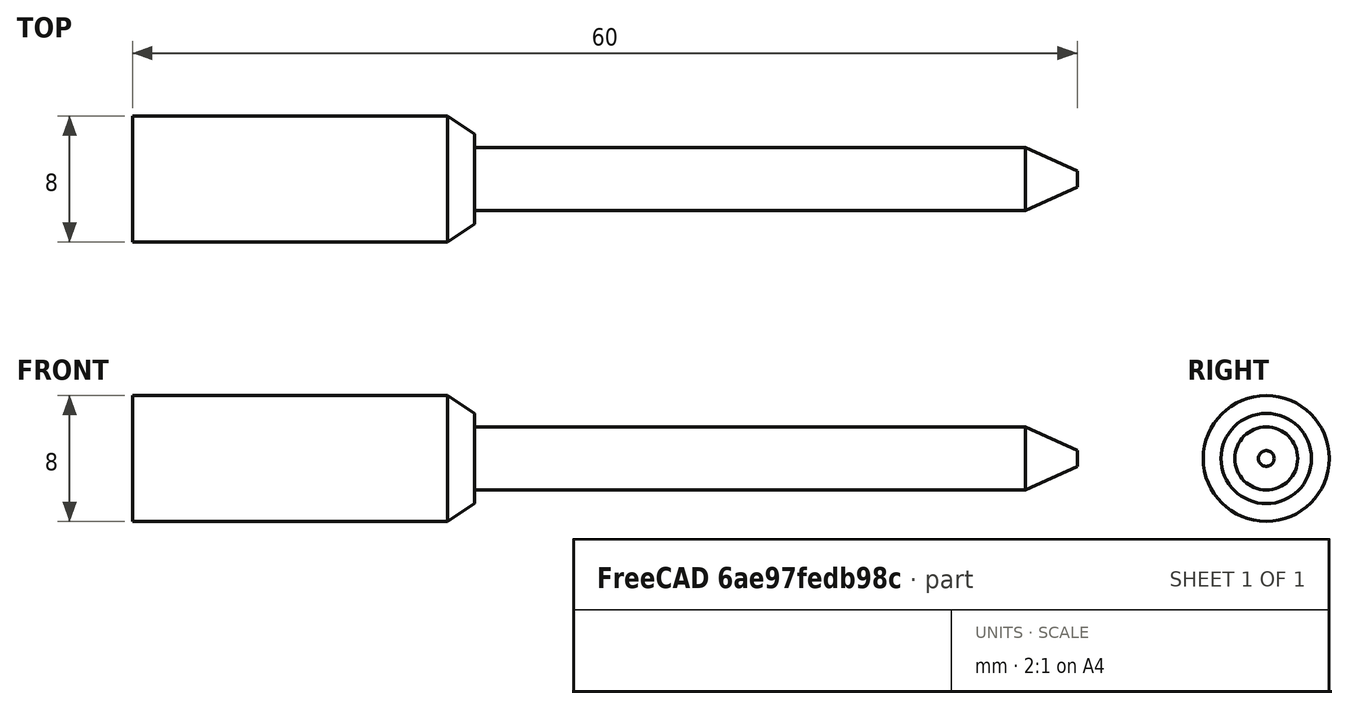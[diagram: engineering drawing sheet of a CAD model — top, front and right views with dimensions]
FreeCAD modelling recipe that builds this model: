
FCSTD DOCUMENT  (FreeCAD 0.18.4R)
Label: gauge-tip
License: All rights reserved
LicenseURL: http://en.wikipedia.org/wiki/All_rights_reserved
objects: Sketcher::SketchObject×1, PartDesign::Revolution×1, PartDesign::Body×1
note: 4 computed .brp shape members not serialized (recipe doc carries the construction recipe); baked Part::Feature solids carry a one-line shape summary decoded from their .brp

FEATURE [Sketcher::SketchObject] Sketch
  MapMode = 5
  Placement = pos=(0,0,0) rot=(1,0,0;1.5708rad)
  Support = -> [XZ_Plane]
  sketch-geometry (8):
    g0: LineSegment StartX=0 StartY=-4 StartZ=0 EndX=20 EndY=-4 EndZ=0
    g1: LineSegment StartX=20 StartY=-4 StartZ=0 EndX=21.7055 EndY=-2.86946 EndZ=0
    g2: LineSegment StartX=21.7055 StartY=-2 StartZ=0 EndX=56.7055 EndY=-2 EndZ=0
    g3: LineSegment StartX=56.7055 StartY=-2 StartZ=0 EndX=60 EndY=-0.5 EndZ=0
    g4: LineSegment StartX=60 StartY=-0.5 StartZ=0 EndX=60 EndY=0 EndZ=0
    g5: LineSegment StartX=60 StartY=0 StartZ=0 EndX=0 EndY=0 EndZ=0
    g6: LineSegment StartX=0 StartY=0 StartZ=0 EndX=0 EndY=-4 EndZ=0
    g7: LineSegment StartX=21.7055 StartY=-2 StartZ=0 EndX=21.7055 EndY=-2.86946 EndZ=0
  constraints (21):
    c: Horizontal(g0)
    c: Coincident(g0,g1)
    c: Horizontal(g2)
    c: Coincident(g2,g3)
    c: Coincident(g3,g4)
    c: PointOnObject(g4,g-1)
    c: Vertical(g4)
    c: Coincident(g4,g5)
    c: Coincident(g5,g-1)
    c: Coincident(g5,g6)
    c: Coincident(g6,g0)
    c: Vertical(g6)
    c: DistanceX(g5,g5) = 60
    c: DistanceX(g0,g0) = 20
    c: DistanceX(g2,g2) = 35
    c: DistanceY(g4,g4) = 0.5
    c: DistanceY(g6,g6) = 4
    c: Coincident(g7,g2)
    c: Coincident(g7,g1)
    c: Vertical(g7)
    c: DistanceY(g2,g4) = 2
FEATURE [PartDesign::Revolution] Revolution
  Angle = 360
  Axis = (1,0,0)
  Base = (0,0,0)
  Placement = pos=(0,0,0) rot=(1,0,0;1.5708rad)
  Profile = -> Sketch
  ReferenceAxis = -> X_Axis
  Reversed = true
FEATURE [PartDesign::Body] Body
  Group = -> [Sketch,Revolution]
  Origin = -> Origin
  Tip = -> Revolution
